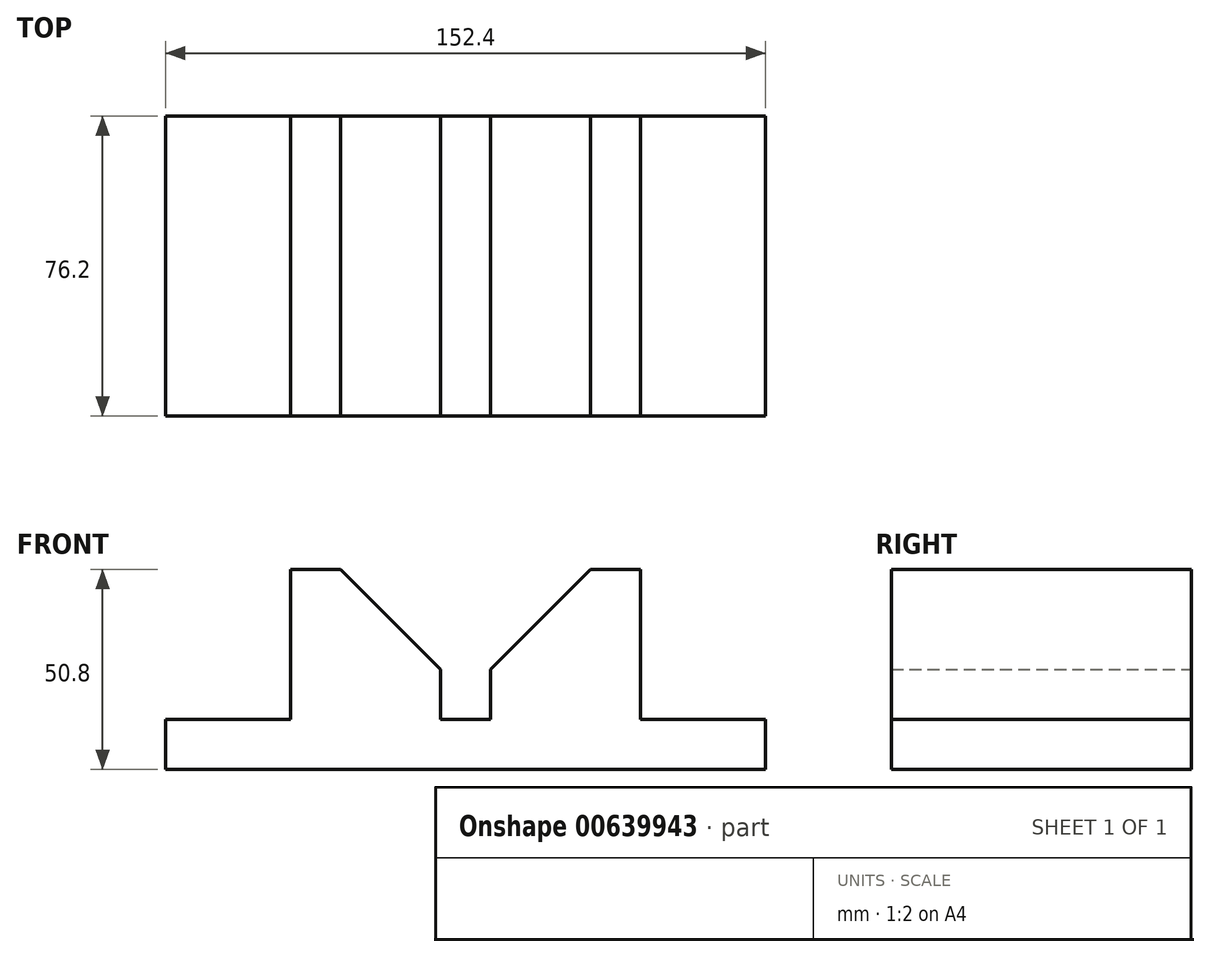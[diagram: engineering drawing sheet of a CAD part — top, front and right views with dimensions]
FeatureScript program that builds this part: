
annotation { "Feature Type Name" : "Feature", "Feature Type Description" : "" }
export const myFeature = defineFeature(function(context is Context, id is Id, definition is map)
    precondition{}
    {
        {
            var Q0;
            Q0=qCreatedBy(makeId("Front.planeOp"),FACE);
            var sketch = newSketch(context, id + "F0", { "sketchPlane" : qUnion([Q0])});
            skLineSegment(sketch, "E0", {"start": v(0, 0) * mm, "end": v(-152.4, 0) * mm});
            skLineSegment(sketch, "E1", {"start": v(-152.4, 0) * mm, "end": v(-152.4, 12.7) * mm});
            skLineSegment(sketch, "E2", {"start": v(0, 0) * mm, "end": v(0, 12.7) * mm});
            skLineSegment(sketch, "E3", {"start": v(0, 12.7) * mm, "end": v(-31.75, 12.7) * mm});
            skLineSegment(sketch, "E4", {"start": v(-152.4, 12.7) * mm, "end": v(-120.65, 12.7) * mm});
            skLineSegment(sketch, "E5", {"start": v(-31.75, 12.7) * mm, "end": v(-31.75, 50.8) * mm});
            skLineSegment(sketch, "E6", {"start": v(-120.65, 12.7) * mm, "end": v(-120.65, 50.8) * mm});
            skLineSegment(sketch, "E7", {"start": v(-120.65, 50.8) * mm, "end": v(-107.95, 50.8) * mm});
            skLineSegment(sketch, "E8", {"start": v(-31.75, 50.8) * mm, "end": v(-44.45, 50.8) * mm});
            skLineSegment(sketch, "E9", {"start": v(-82.55, 0) * mm, "end": v(-69.85, 0) * mm});
            skLineSegment(sketch, "E10", {"start": v(-82.55, 12.7) * mm, "end": v(-69.85, 12.7) * mm});
            skLineSegment(sketch, "E11", {"start": v(-69.85, 12.7) * mm, "end": v(-69.85, 25.4) * mm});
            skLineSegment(sketch, "E12", {"start": v(-82.55, 12.7) * mm, "end": v(-82.55, 25.4) * mm});
            skLineSegment(sketch, "E13", {"start": v(-82.55, 25.4) * mm, "end": v(-107.95, 50.8) * mm});
            skLineSegment(sketch, "E14", {"start": v(-69.85, 25.4) * mm, "end": v(-44.45, 50.8) * mm});
            skSolve(sketch);
        }
        {
            var Q0;
            Q0 = qSketchRegion(id + "F0", true);
            extrude(context, id + "F1", {"entities" : qUnion([Q0]), "depth" : 76.2 * mm, "offsetDistance" : 25.4 * mm});
        }
    });
